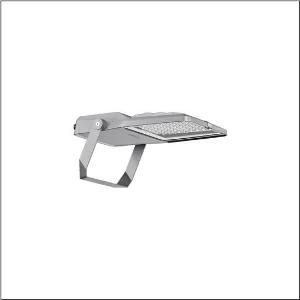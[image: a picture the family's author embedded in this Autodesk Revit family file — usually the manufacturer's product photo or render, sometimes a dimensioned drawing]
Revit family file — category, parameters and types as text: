
# Revit family: floodlight_fl_21_mini___pl43_5xa7776b2a1a_e86b
name_source: partatom
category: Lighting Fixtures
units: mm (PartAtom-declared; Revit-internal decimal feet)

## family parameters
Cut with Voids When Loaded = No
Host = Face
Light Source = No
Part Type = Normal
Room Calculation Point = No
Round Connector Dimension = Use Diameter
Shared = No

## types (1)
- --- (1 x LED, 6390 lm, 45.7 W, 3000K)
    Apparent Load = 46 VA
    CIE Flux Codes = 27 78 99 100 100
    Color Rendering = 70
    Color Temperature = 3000K
    Default Elevation = 1800 mm
    Description = Floodlight FL 21 mini, floodlight, primary light control with lens, of PMMA, primary optical cover: protective disc, of toughened safety glass, transparent, light distribution: PL43, light emission: direct distribution, installation type: surface-mounted, LED, High Power LED, rated luminous flux: 6.390lm, luminous efficacy: 140lm/W, light colour: 730, colour temperature: 3000K, control: flexible luminous flux parameterisation, time-dependent luminous flux control, constant luminous flux control, overheat protection, presetting dimming logarithmic, with terminal, 6-pole, mains connection: 220..240V, AC, 50/60Hz, start of lifetime: 46W, end of service life: 48W, reduction: 22W, luminaire housing, of diecast aluminium, powder-coated, Siteco® metallic grey (DB 702S), corrosivity category C5 mid according to DIN EN ISO 12944, sealing non-destructively replaceable, mounting bracket, of steel, galvanised, powder-coated, Siteco® metallic grey (DB 702S), Smart Interface below and above, protection rating (complete): IP66, insulation class (complete): insulation class II (safety insulation), certification: CE, ENEC, VDE, protection symbol: D, impact resistance: IK08, permissible operating ambient temperature: -40..+40°C, permissible operating ambient temperature for outdoor applications: -40..+50°C, standard: DIN EN 12944, LABS conformity tested according to VDMA 24364:2018-05, packaging unit: 1 piece

Light Distribution: PL43
    Height = 70 mm
    Lamp = 1 x LED
    Lamp Light Flux = 6390 lm
    Lamp Power = 45.7 W
    Lamp count = 1
    Length = 485 mm
    Luminous efficacy = 140 lm/W
    Manufacturer = Siteco
    ModVariant = No
    Model = 5XA7776B2A1A
    Number of Poles = 1
    OnlyDefault = Yes
    Power Factor = 1
    Product Name = Floodlight FL 21 mini | PL43
    Product group = floodlight | pylon annexe
    ProductGroupID = 6200
    Protection Class = Protection class II
    Protection Degree = IP 66
    RLX_Detail_Level = 1
    RLX_Emergency_Light_Flux = 0 lm
    RLX_Emergency_Type = 0
    RLX_Emergency_Type_DB = No
    RlxData = <blob elided: 95821 chars, md5=ebd8a763>
    Socket = socket
    Standby Power = 0 W
    System Light Flux = 6390 lm
    System Power = 46 W
    Type Comments = factory setting: luminous flux: 100 % | dim-lin: 254 | 463 mA
    Type Image = l_1006845.jpg
    URL = http://relux.com
    VarID = @adj_111443
    Voltage = 0 V
    Weight = 0.00 kg
    Width = 337 mm

## geometry (parser evidence)
native form markers: Blend x4, Sweep x13
no freeform markers — native parametric forms only
